# Revit family: LBC6-P
name_source: partatom
category: Lighting Fixtures
revit_build: Autodesk Revit 2014 (Build: 20130308_1515(x64)
units: mm (PartAtom-declared; Revit-internal decimal feet)

## types (5) — shared parameters
Apparent Load = 0 VA
Color Filter = 16777215
Default Elevation = 48"
Description = Nominal 6in cylinders designed to be used with the LiteBox LB6LEDA series trims
Dimming Lamp Color Temperature Shift = <None>
Emit Shape Visible in Rendering = No
Emit from Circle Diameter = 3"
Lamp = LED Lamp
Load Classification = Lighting
Manufacturer = Prescolite
Model = LBC6
Photometric Web File = LB6LEDA10L-27K.ies
Photometric Wen Link = https://www.hubbell.com
Product Documentation Link = https://hubbellcdn.com
Product Page URL = https://www.hubbell.com
Reflector = Hubbell - White
Tilt Angle = -90.00°
URL = https://www.hubbell.com
Voltage = 120 V
Wattage Comments = 12W

## per-type parameters (varying)
| type | Ballast |
| LBC6-WH | Hubbell - White |
| LBC6-BL | Hubbell - Black |
| LBC6-Z | Hubbell - Zet |
| LBC6-BA | Hubbell - Aluminium |
| LBC6-BZ | Hubbell - Bronze |

## geometry (parser evidence)
native form markers: Blend x10, Sweep x2
no freeform markers — native parametric forms only
